# Revit family: Faucet-Handle-KOHLER-Components-K-77963
name_source: partatom
category: Plumbing Fixtures
revit_build: Autodesk Revit 2015 (Build: 20140606_1530(x64)
units: mm (PartAtom-declared; Revit-internal decimal feet)

## types (3) — shared parameters
ADA Compliant = Yes
Assembly Code = D2010
CW Connection = Yes
Cold Water Inlet = Cold Water Inlet
Date Modified = 07/03/2018
Default Elevation = 36"
Description = Remote Valve Bathroom Sink Faucet Handle
Drain Included = No
Flow Rate = 0 GPM
HW Connection = Yes
Handle Clearance = 1 3/16"
Height = 1 3/16"
Hot Water Inlet = Hot Water Inlet
Length = 2 3/8"
Manufacturer = KOHLER Co.
MasterFormat 1995 = 15410
MasterFormat 2004 = 22.41.39
Material = Premium Metal Construction
Pressure = 0.00 psi
Product Documentation Link = http://www.us.kohler.com
Product Name = Components
Product Page URL = http://www.us.kohler.com
URL = https://www.us.kohler.com
Vent Connection = No
Waste Connection = No
Waste Water Outlet = Waste Water Outlet
Width = 2 3/8"

## per-type parameters (varying)
| type | Finish | Model | Type |
| CP-Polished Chrome | Kohler-Metal-CP-Polished_Chrome | K-77963-8A-CP | 1 |
| BL-Matte black | Kohler-Metal-BL-Matte_Black | K-77963-8A-BL | 2 |
| TT-Vibrant Titanium | Kohler-Metal-TT-Vibrant_Titanium | K-77963-8A-TT | 3 |

## geometry (parser evidence)
native form markers: Sweep x6
no freeform markers — native parametric forms only
